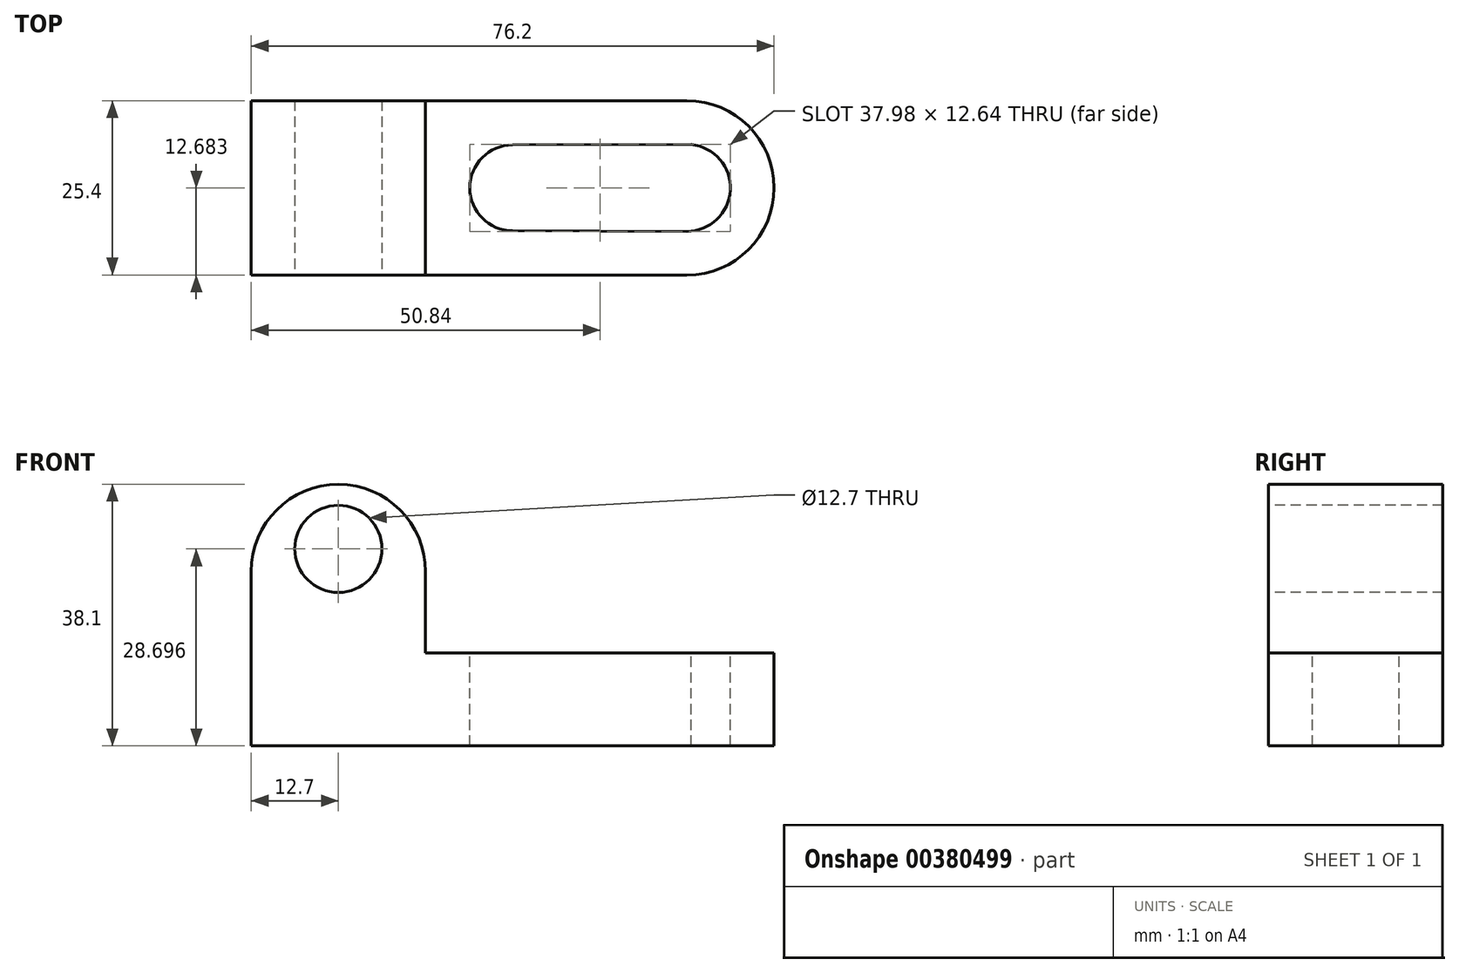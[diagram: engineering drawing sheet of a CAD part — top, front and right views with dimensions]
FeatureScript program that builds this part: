
annotation { "Feature Type Name" : "Feature", "Feature Type Description" : "" }
export const myFeature = defineFeature(function(context is Context, id is Id, definition is map)
    precondition{}
    {
        {
            var Q0;
            Q0=qCreatedBy(makeId("Front.planeOp"),FACE);
            var sketch = newSketch(context, id + "F0", { "sketchPlane" : qUnion([Q0])});
            skLineSegment(sketch, "E0", {"start": v(0, 0) * mm, "end": v(76.2, 0) * mm});
            skLineSegment(sketch, "E1", {"start": v(76.2, 0) * mm, "end": v(76.2, 38.1) * mm});
            skLineSegment(sketch, "E2", {"start": v(76.2, 38.1) * mm, "end": v(0, 38.1) * mm});
            skLineSegment(sketch, "E3", {"start": v(0, 38.1) * mm, "end": v(0, 0) * mm});
            skSolve(sketch);
        }
        {
            var Q0;
            Q0=makeQuery(id+"F0.imprint","IMPRINT",FACE,{"disambiguationData":[TD([[makeQuery(id+"F0.imprint","IMPRINT",EDGE,{"derivedFrom":sQuery(id+"F0.wireOp",EDGE,"E0")}),1.0]])]});
            extrude(context, id + "F1", {"entities" : qUnion([Q0]), "depth" : 25.4 * mm});
        }
        {
            var Q0;
            Q0=makeQuery(id+"F1.opExtrude","CAP_FACE",FACE,{"disambiguationData":[OSD([sQuery(id+"F0.wireOp",EDGE,"E0"),sQuery(id+"F0.wireOp",EDGE,"E1"),sQuery(id+"F0.wireOp",EDGE,"E2"),sQuery(id+"F0.wireOp",EDGE,"E3")])],"isStart":false});
            var sketch = newSketch(context, id + "F2", { "sketchPlane" : qUnion([Q0])});
            skLineSegment(sketch, "E4", {"start": v(25.4, 38.1) * mm, "end": v(25.4, 13.5) * mm});
            skLineSegment(sketch, "E5", {"start": v(25.4, 13.5) * mm, "end": v(76.2, 13.5) * mm});
            skSolve(sketch);
        }
        {
            var Q0;
            {var subQ0=sQuery(id+"F2.wireOp",EDGE,"E4");Q0=makeQuery(id+"F2.imprint","IMPRINT",FACE,{"disambiguationData":[TD([[makeQuery(id+"F2.imprint","IMPRINT",EDGE,{"derivedFrom":subQ0}),1.0]])]});}
            extrude(context, id + "F3", {"entities" : qUnion([Q0]), "operationType" : NewBodyOperationType.REMOVE, "oppositeDirection" : true, "depth" : 25.4 * mm});
        }
        {
            var Q0;
            Q0=makeQuery(id+"F1.opExtrude","CAP_FACE",FACE,{"disambiguationData":[OSD([sQuery(id+"F0.wireOp",EDGE,"E0"),sQuery(id+"F0.wireOp",EDGE,"E1"),sQuery(id+"F0.wireOp",EDGE,"E2"),sQuery(id+"F0.wireOp",EDGE,"E3")])],"isStart":false});
            var sketch = newSketch(context, id + "F4", { "sketchPlane" : qUnion([Q0])});
            skCircle(sketch, "E6", {"center": v(12.7, 28.7) * mm, "radius": 6.35 * mm});
            skSolve(sketch);
        }
        {
            var Q0;
            Q0=makeQuery(id+"F4.imprint","IMPRINT",FACE,{"disambiguationData":[TD([[makeQuery(id+"F4.imprint","IMPRINT",EDGE,{"derivedFrom":sQuery(id+"F4.wireOp",EDGE,"E6")}),1.0]])]});
            extrude(context, id + "F5", {"entities" : qUnion([Q0]), "operationType" : NewBodyOperationType.REMOVE, "oppositeDirection" : true, "depth" : 25.4 * mm});
        }
        {
            var Q0;
            Q0=makeQuery(id+"F1.opExtrude","CAP_FACE",FACE,{"disambiguationData":[OSD([sQuery(id+"F0.wireOp",EDGE,"E0"),sQuery(id+"F0.wireOp",EDGE,"E1"),sQuery(id+"F0.wireOp",EDGE,"E2"),sQuery(id+"F0.wireOp",EDGE,"E3")])],"isStart":false});
            var sketch = newSketch(context, id + "F6", { "sketchPlane" : qUnion([Q0])});
            skArc(sketch, "E7", {"start": v(25.4, 25.4) * mm, "mid": v(12.7, 38.1) * mm, "end": v(0, 25.4) * mm});
            skSolve(sketch);
        }
        {
            var Q0;
            {var subQ0=sQuery(id+"F6.wireOp",EDGE,"E7");var subQ1=makeQuery(id+"F1.opExtrude","CAP_EDGE",EDGE,{"disambiguationData":[OSD([sQuery(id+"F0.wireOp",EDGE,"E3")])],"isStart":false});var subQ2=makeQuery(id+"F6.imprint","INTERSECT",VERTEX,{"derivedFrom":[subQ1,subQ0]});Q0=makeQuery(id+"F6.imprint","IMPRINT",FACE,{"disambiguationData":[TD([[makeQuery(id+"F6.imprint","IMPRINT",EDGE,{"disambiguationData":[TD([[subQ2,1.0]])],"derivedFrom":subQ0}),-1.0]])]});}
            var Q1;
            {var subQ0=sQuery(id+"F6.wireOp",EDGE,"E7");var subQ1=makeQuery(id+"F3.boolean.opBoolean","COPY",EDGE,{"derivedFrom":makeQuery(id+"F3.opExtrude","CAP_EDGE",EDGE,{"disambiguationData":[OSD([sQuery(id+"F2.wireOp",EDGE,"E4")])],"isStart":true})});var subQ2=makeQuery(id+"F6.imprint","INTERSECT",VERTEX,{"derivedFrom":[subQ1,subQ0]});Q1=makeQuery(id+"F6.imprint","IMPRINT",FACE,{"disambiguationData":[TD([[makeQuery(id+"F6.imprint","IMPRINT",EDGE,{"disambiguationData":[TD([[subQ2,-1.0]])],"derivedFrom":subQ0}),-1.0]])]});}
            extrude(context, id + "F7", {"entities" : qUnion([Q0, Q1]), "operationType" : NewBodyOperationType.REMOVE, "oppositeDirection" : true, "depth" : 25.4 * mm});
        }
        {
            var Q0;
            Q0=makeQuery(id+"F3.boolean.opBoolean","COPY",FACE,{"derivedFrom":makeQuery(id+"F3.opExtrude","SWEPT_FACE",FACE,{"disambiguationData":[OSD([sQuery(id+"F2.wireOp",EDGE,"E5")])]})});
            var sketch = newSketch(context, id + "F8", { "sketchPlane" : qUnion([Q0])});
            skArc(sketch, "E8", {"start": v(63.5, -25.4) * mm, "mid": v(76.2, -12.7) * mm, "end": v(63.5, 0) * mm});
            skSolve(sketch);
        }
        {
            var Q0;
            {var subQ0=sQuery(id+"F8.wireOp",EDGE,"E8");var subQ1=sQuery(id+"F2.wireOp",EDGE,"E5");var subQ2=makeQuery(id+"F3.boolean.opBoolean","COPY",EDGE,{"derivedFrom":makeQuery(id+"F3.opExtrude","CAP_EDGE",EDGE,{"disambiguationData":[OSD([subQ1])],"isStart":false})});var subQ3=makeQuery(id+"F8.imprint","INTERSECT",VERTEX,{"derivedFrom":[subQ2,subQ0]});Q0=makeQuery(id+"F8.imprint","IMPRINT",FACE,{"disambiguationData":[TD([[makeQuery(id+"F8.imprint","IMPRINT",EDGE,{"disambiguationData":[TD([[subQ3,1.0]])],"derivedFrom":subQ0}),-1.0]])]});}
            var Q1;
            {var subQ0=sQuery(id+"F8.wireOp",EDGE,"E8");var subQ1=sQuery(id+"F2.wireOp",EDGE,"E5");var subQ2=makeQuery(id+"F3.boolean.opBoolean","COPY",EDGE,{"derivedFrom":makeQuery(id+"F3.opExtrude","CAP_EDGE",EDGE,{"disambiguationData":[OSD([subQ1])],"isStart":true})});var subQ3=makeQuery(id+"F8.imprint","INTERSECT",VERTEX,{"derivedFrom":[subQ2,subQ0]});Q1=makeQuery(id+"F8.imprint","IMPRINT",FACE,{"disambiguationData":[TD([[makeQuery(id+"F8.imprint","IMPRINT",EDGE,{"disambiguationData":[TD([[subQ3,-1.0]])],"derivedFrom":subQ0}),-1.0]])]});}
            extrude(context, id + "F9", {"entities" : qUnion([Q0, Q1]), "operationType" : NewBodyOperationType.REMOVE, "oppositeDirection" : true, "depth" : 25.4 * mm});
        }
        {
            var Q0;
            Q0=makeQuery(id+"F3.boolean.opBoolean","COPY",FACE,{"derivedFrom":makeQuery(id+"F3.opExtrude","SWEPT_FACE",FACE,{"disambiguationData":[OSD([sQuery(id+"F2.wireOp",EDGE,"E5")])]})});
            var sketch = newSketch(context, id + "F10", { "sketchPlane" : qUnion([Q0])});
            skCircle(sketch, "E9", {"center": v(63.5, -12.7) * mm, "radius": 6.34 * mm});
            skCircle(sketch, "E10", {"center": v(38.11, -12.7) * mm, "radius": 6.26 * mm});
            skLineSegment(sketch, "E11", {"start": v(64.14, -6.4) * mm, "end": v(38.1, -6.44) * mm});
            skLineSegment(sketch, "E12", {"start": v(38.1, -18.96) * mm, "end": v(63.48, -19.04) * mm});
            skSolve(sketch);
        }
        {
            var Q0;
            {var subQ0=sQuery(id+"F10.wireOp",EDGE,"E9");var subQ1=makeQuery(id+"F10.imprint","INTERSECT",VERTEX,{"derivedFrom":[subQ0,sQuery(id+"F10.wireOp",EDGE,"E12")]});Q0=makeQuery(id+"F10.imprint","IMPRINT",FACE,{"disambiguationData":[TD([[makeQuery(id+"F10.imprint","IMPRINT",EDGE,{"disambiguationData":[TD([[subQ1,1.0]])],"derivedFrom":subQ0}),1.0]])]});}
            var Q1;
            {var subQ0=sQuery(id+"F10.wireOp",EDGE,"E12");Q1=makeQuery(id+"F10.imprint","IMPRINT",FACE,{"disambiguationData":[TD([[makeQuery(id+"F10.imprint","IMPRINT",EDGE,{"derivedFrom":subQ0}),1.0]])]});}
            var Q2;
            {var subQ0=sQuery(id+"F10.wireOp",EDGE,"E10");var subQ1=makeQuery(id+"F10.imprint","INTERSECT",VERTEX,{"derivedFrom":[subQ0,sQuery(id+"F10.wireOp",EDGE,"E11")]});Q2=makeQuery(id+"F10.imprint","IMPRINT",FACE,{"disambiguationData":[TD([[makeQuery(id+"F10.imprint","IMPRINT",EDGE,{"disambiguationData":[TD([[subQ1,-1.0]])],"derivedFrom":subQ0}),1.0]])]});}
            extrude(context, id + "F11", {"entities" : qUnion([Q0, Q1, Q2]), "operationType" : NewBodyOperationType.REMOVE, "oppositeDirection" : true, "depth" : 25.4 * mm});
        }
    });
